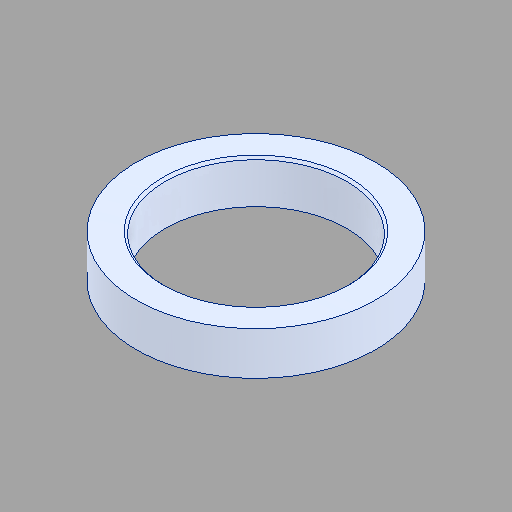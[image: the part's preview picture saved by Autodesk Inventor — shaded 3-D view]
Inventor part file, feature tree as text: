
AUTODESK INVENTOR PART (.ipt)
format: ipt  version: 2024.2 (Build 282272000, 272)  size: 95,232 bytes
history: native  units: in
note: dims shown in document units (in); Inventor stores cm internally (conversion verified against a paired STEP export)
features: chamfer x1
ambient origin geometry x8: Origin, YZ Plane, XZ Plane, XY Plane, X Axis, Y Axis, Z Axis, Center Point
bodies: Solid1 (feature_tree)
feature tree (1):
  chamfer  "Chamfer1"  [1 undecoded]
note: 1 required parameter value undecoded (feature->parameter linkage not recoverable at this tier; creation-order binding heuristic only, values carry confidence <= 0.55)
